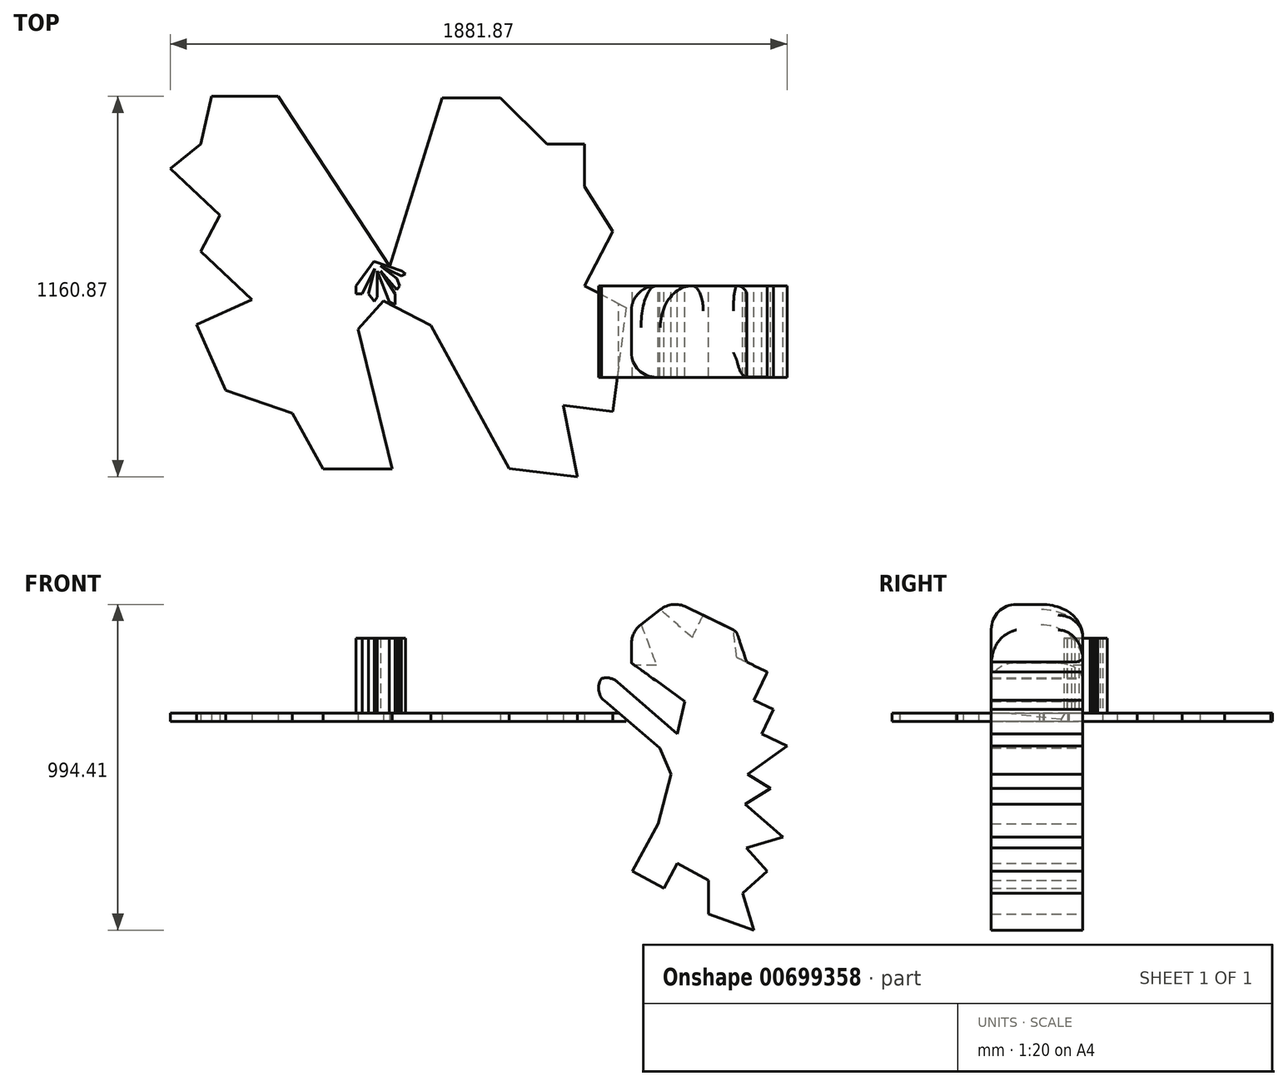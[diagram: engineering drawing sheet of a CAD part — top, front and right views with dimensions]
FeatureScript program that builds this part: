
annotation { "Feature Type Name" : "Feature", "Feature Type Description" : "" }
export const myFeature = defineFeature(function(context is Context, id is Id, definition is map)
    precondition{}
    {
        {
            var Q0;
            Q0=qCreatedBy(makeId("Top.planeOp"),FACE);
            var sketch = newSketch(context, id + "F0", { "sketchPlane" : qUnion([Q0])});
            skLineSegment(sketch, "E0", {"start": v(-30.37, 73.87) * mm, "end": v(-84.93, 0) * mm});
            skLineSegment(sketch, "E1", {"start": v(-84.93, 0) * mm, "end": v(-84.93, -24.22) * mm});
            skLineSegment(sketch, "E2", {"start": v(-84.93, -24.22) * mm, "end": v(-65.9, -24.22) * mm});
            skLineSegment(sketch, "E3", {"start": v(-65.9, -24.22) * mm, "end": v(-27.47, 52.56) * mm});
            skLineSegment(sketch, "E4", {"start": v(-27.47, 52.56) * mm, "end": v(-45.92, -24.95) * mm});
            skLineSegment(sketch, "E5", {"start": v(-45.92, -24.95) * mm, "end": v(-28.38, -47.2) * mm});
            skLineSegment(sketch, "E6", {"start": v(-28.38, -47.2) * mm, "end": v(-19.48, -35.16) * mm});
            skLineSegment(sketch, "E7", {"start": v(-19.48, -35.16) * mm, "end": v(-19.48, 44.64) * mm});
            skLineSegment(sketch, "E8", {"start": v(-19.48, 44.64) * mm, "end": v(16.74, -49.35) * mm});
            skLineSegment(sketch, "E9", {"start": v(16.74, -49.35) * mm, "end": v(35.46, -57.35) * mm});
            skLineSegment(sketch, "E10", {"start": v(35.46, -57.35) * mm, "end": v(35.46, -24.95) * mm});
            skLineSegment(sketch, "E11", {"start": v(35.46, -24.95) * mm, "end": v(-9.72, 44.64) * mm});
            skLineSegment(sketch, "E12", {"start": v(-9.72, 44.64) * mm, "end": v(40.42, -11.66) * mm});
            skLineSegment(sketch, "E13", {"start": v(40.42, -11.66) * mm, "end": v(49.03, 0) * mm});
            skLineSegment(sketch, "E14", {"start": v(49.03, 0) * mm, "end": v(40.42, 22.8) * mm});
            skLineSegment(sketch, "E15", {"start": v(40.42, 22.8) * mm, "end": v(-9.72, 59.82) * mm});
            skLineSegment(sketch, "E16", {"start": v(-9.72, 59.82) * mm, "end": v(53.76, 29.47) * mm});
            skLineSegment(sketch, "E17", {"start": v(53.76, 29.47) * mm, "end": v(67.14, 36.15) * mm});
            skLineSegment(sketch, "E18", {"start": v(67.14, 36.15) * mm, "end": v(55.65, 44.64) * mm});
            skLineSegment(sketch, "E19", {"start": v(55.65, 44.64) * mm, "end": v(-30.37, 73.87) * mm});
            skCircle(sketch, "E20", {"center": v(848.67, 52.41) * mm, "radius": 262.45 * mm});
            skCircle(sketch, "E21", {"center": v(612.08, -61.18) * mm, "radius": 272.09 * mm});
            skSolve(sketch);
        }
        {
            var Q0;
            Q0=makeQuery(id+"F0.imprint","IMPRINT",FACE,{"disambiguationData":[TD([[makeQuery(id+"F0.imprint","IMPRINT",EDGE,{"derivedFrom":sQuery(id+"F0.wireOp",EDGE,"E0")}),1.0]])]});
            extrude(context, id + "F1", {"entities" : qUnion([Q0]), "depth" : 254 * mm, "offsetDistance" : 25.4 * mm});
        }
        {
            var Q0;
            Q0=qCreatedBy(makeId("Top.planeOp"),FACE);
            var sketch = newSketch(context, id + "F2", { "sketchPlane" : qUnion([Q0])});
            skLineSegment(sketch, "E22", {"start": v(0, 0) * mm, "end": v(178.34, 573.44) * mm});
            skLineSegment(sketch, "E23", {"start": v(178.34, 573.44) * mm, "end": v(356.71, 573.44) * mm});
            skLineSegment(sketch, "E24", {"start": v(356.71, 573.44) * mm, "end": v(498.38, 432.3) * mm});
            skLineSegment(sketch, "E25", {"start": v(498.38, 432.3) * mm, "end": v(612.76, 432.3) * mm});
            skLineSegment(sketch, "E26", {"start": v(612.76, 432.3) * mm, "end": v(612.76, 303.27) * mm});
            skLineSegment(sketch, "E27", {"start": v(612.76, 303.27) * mm, "end": v(699.5, 165.4) * mm});
            skLineSegment(sketch, "E28", {"start": v(699.5, 165.4) * mm, "end": v(612.76, 0) * mm});
            skLineSegment(sketch, "E29", {"start": v(612.76, 0) * mm, "end": v(739.89, -66.67) * mm});
            skLineSegment(sketch, "E30", {"start": v(739.89, -66.67) * mm, "end": v(699.5, -384.6) * mm});
            skLineSegment(sketch, "E31", {"start": v(699.5, -384.6) * mm, "end": v(548.24, -365.4) * mm});
            skLineSegment(sketch, "E32", {"start": v(548.24, -365.4) * mm, "end": v(590.6, -582.87) * mm});
            skLineSegment(sketch, "E33", {"start": v(590.6, -582.87) * mm, "end": v(383.14, -558.17) * mm});
            skLineSegment(sketch, "E34", {"start": v(383.14, -558.17) * mm, "end": v(144.45, -121.46) * mm});
            skLineSegment(sketch, "E35", {"start": v(144.45, -121.46) * mm, "end": v(0, -45.7) * mm});
            skLineSegment(sketch, "E36", {"start": v(0, -45.7) * mm, "end": v(-77.82, -132.2) * mm});
            skLineSegment(sketch, "E37", {"start": v(-77.82, -132.2) * mm, "end": v(26.03, -559.4) * mm});
            skLineSegment(sketch, "E38", {"start": v(26.03, -559.4) * mm, "end": v(-184.42, -559.4) * mm});
            skLineSegment(sketch, "E39", {"start": v(-184.42, -559.4) * mm, "end": v(-278.79, -389.33) * mm});
            skLineSegment(sketch, "E40", {"start": v(-278.79, -389.33) * mm, "end": v(-482.47, -318.78) * mm});
            skLineSegment(sketch, "E41", {"start": v(-482.47, -318.78) * mm, "end": v(-571.43, -118.15) * mm});
            skLineSegment(sketch, "E42", {"start": v(-571.43, -118.15) * mm, "end": v(-402.06, -43.06) * mm});
            skLineSegment(sketch, "E43", {"start": v(-402.06, -43.06) * mm, "end": v(-557.53, 105.32) * mm});
            skLineSegment(sketch, "E44", {"start": v(-557.53, 105.32) * mm, "end": v(-499.66, 215.66) * mm});
            skLineSegment(sketch, "E45", {"start": v(-499.66, 215.66) * mm, "end": v(-651.09, 357.06) * mm});
            skLineSegment(sketch, "E46", {"start": v(-651.09, 357.06) * mm, "end": v(-557.53, 432.3) * mm});
            skLineSegment(sketch, "E47", {"start": v(-557.53, 432.3) * mm, "end": v(-524.67, 578) * mm});
            skLineSegment(sketch, "E48", {"start": v(-524.67, 578) * mm, "end": v(-322.06, 578) * mm});
            skLineSegment(sketch, "E49", {"start": v(-322.06, 578) * mm, "end": v(18.58, 59.74) * mm});
            skSolve(sketch);
        }
        {
            var Q0;
            {var subQ0=sQuery(id+"F2.wireOp",EDGE,"E23");Q0=makeQuery(id+"F2.imprint","IMPRINT",FACE,{"disambiguationData":[TD([[makeQuery(id+"F2.imprint","IMPRINT",EDGE,{"derivedFrom":subQ0}),-1.0]])]});}
            extrude(context, id + "F3", {"entities" : qUnion([Q0]), "operationType" : NewBodyOperationType.ADD, "depth" : 25.4 * mm, "offsetDistance" : 25.4 * mm});
        }
        {
            var Q0;
            Q0=qCreatedBy(makeId("Front.planeOp"),FACE);
            var sketch = newSketch(context, id + "F4", { "sketchPlane" : qUnion([Q0])});
            skLineSegment(sketch, "E50", {"start": v(1076.45, 274.56) * mm, "end": v(881.65, 370.25) * mm});
            skLineSegment(sketch, "E51", {"start": v(881.65, 370.25) * mm, "end": v(755.9, 273.4) * mm});
            skLineSegment(sketch, "E52", {"start": v(755.9, 273.4) * mm, "end": v(755.9, 178.66) * mm});
            skLineSegment(sketch, "E53", {"start": v(755.9, 178.66) * mm, "end": v(918.64, 61.21) * mm});
            skLineSegment(sketch, "E54", {"start": v(918.64, 61.21) * mm, "end": v(896.44, -38.41) * mm});
            skLineSegment(sketch, "E55", {"start": v(896.44, -38.41) * mm, "end": v(691.79, 139.03) * mm});
            skLineSegment(sketch, "E56", {"start": v(691.79, 139.03) * mm, "end": v(612.88, 114.95) * mm});
            skLineSegment(sketch, "E57", {"start": v(612.88, 114.95) * mm, "end": v(842.2, -81.93) * mm});
            skLineSegment(sketch, "E58", {"start": v(842.2, -81.93) * mm, "end": v(876.72, -160.94) * mm});
            skLineSegment(sketch, "E59", {"start": v(876.72, -160.94) * mm, "end": v(837.27, -312.29) * mm});
            skLineSegment(sketch, "E60", {"start": v(837.27, -312.29) * mm, "end": v(758.36, -457.18) * mm});
            skLineSegment(sketch, "E61", {"start": v(758.36, -457.18) * mm, "end": v(854.94, -509.78) * mm});
            skLineSegment(sketch, "E62", {"start": v(854.94, -509.78) * mm, "end": v(896.44, -433.55) * mm});
            skLineSegment(sketch, "E63", {"start": v(896.44, -433.55) * mm, "end": v(991, -485.05) * mm});
            skLineSegment(sketch, "E64", {"start": v(991, -485.05) * mm, "end": v(991, -588.43) * mm});
            skLineSegment(sketch, "E65", {"start": v(991, -588.43) * mm, "end": v(1129.6, -637.25) * mm});
            skLineSegment(sketch, "E66", {"start": v(1129.6, -637.25) * mm, "end": v(1095.94, -524.12) * mm});
            skLineSegment(sketch, "E67", {"start": v(1095.94, -524.12) * mm, "end": v(1170.57, -457.18) * mm});
            skLineSegment(sketch, "E68", {"start": v(1170.57, -457.18) * mm, "end": v(1107, -386.3) * mm});
            skLineSegment(sketch, "E69", {"start": v(1107, -386.3) * mm, "end": v(1218.74, -353.48) * mm});
            skLineSegment(sketch, "E70", {"start": v(1218.74, -353.48) * mm, "end": v(1103.14, -252.68) * mm});
            skLineSegment(sketch, "E71", {"start": v(1103.14, -252.68) * mm, "end": v(1180.2, -205.09) * mm});
            skLineSegment(sketch, "E72", {"start": v(1180.2, -205.09) * mm, "end": v(1110.37, -160.94) * mm});
            skLineSegment(sketch, "E73", {"start": v(1110.37, -160.94) * mm, "end": v(1230.78, -75.19) * mm});
            skLineSegment(sketch, "E74", {"start": v(1230.78, -75.19) * mm, "end": v(1153.72, -38.41) * mm});
            skLineSegment(sketch, "E75", {"start": v(1153.72, -38.41) * mm, "end": v(1189.4, 36.35) * mm});
            skLineSegment(sketch, "E76", {"start": v(1189.4, 36.35) * mm, "end": v(1129.6, 64.89) * mm});
            skLineSegment(sketch, "E77", {"start": v(1129.6, 64.89) * mm, "end": v(1170.72, 151.05) * mm});
            skLineSegment(sketch, "E78", {"start": v(1170.72, 151.05) * mm, "end": v(1107.85, 181.05) * mm});
            skLineSegment(sketch, "E79", {"start": v(1107.85, 181.05) * mm, "end": v(1076.45, 274.56) * mm});
            skSolve(sketch);
        }
        {
            var Q0;
            Q0=makeQuery(id+"F4.imprint","IMPRINT",FACE,{"disambiguationData":[TD([[makeQuery(id+"F4.imprint","IMPRINT",EDGE,{"derivedFrom":sQuery(id+"F4.wireOp",EDGE,"E50")}),1.0]])]});
            extrude(context, id + "F5", {"entities" : qUnion([Q0]), "operationType" : NewBodyOperationType.ADD, "depth" : 279.4 * mm, "offsetDistance" : 25.4 * mm});
        }
        {
            var Q0;
            Q0=makeQuery(id+"F5.opExtrude","CAP_EDGE",EDGE,{"disambiguationData":[OSD([sQuery(id+"F4.wireOp",EDGE,"E51")])],"isStart":true});
            fillet(context, id + "F6", {"entities" : qUnion([Q0]), "radius" : 127 * mm, "tangentPropagation" : true, "allowEdgeOverflow" : false});
        }
        {
            var Q0;
            Q0=makeQuery(id+"F5.opExtrude","SWEPT_EDGE",EDGE,{"disambiguationData":[OSD([sQuery(id+"F4.wireOp",EDGE,"E51"),sQuery(id+"F4.wireOp",EDGE,"E52")])]});
            fillet(context, id + "F7", {"entities" : qUnion([Q0]), "radius" : 76.2 * mm, "tangentPropagation" : true, "allowEdgeOverflow" : false});
        }
        {
            var Q0;
            Q0=makeQuery(id+"F5.opExtrude","SWEPT_EDGE",EDGE,{"disambiguationData":[OSD([sQuery(id+"F4.wireOp",EDGE,"E50"),sQuery(id+"F4.wireOp",EDGE,"E51")])]});
            fillet(context, id + "F8", {"entities" : qUnion([Q0]), "radius" : 76.2 * mm, "tangentPropagation" : true, "allowEdgeOverflow" : false});
        }
        {
            var Q0;
            Q0=makeQuery(id+"F5.opExtrude","SWEPT_EDGE",EDGE,{"disambiguationData":[OSD([sQuery(id+"F4.wireOp",EDGE,"E50"),sQuery(id+"F4.wireOp",EDGE,"E79")])]});
            fillet(context, id + "F9", {"entities" : qUnion([Q0]), "radius" : 25.4 * mm, "tangentPropagation" : true, "allowEdgeOverflow" : false});
        }
        {
            var Q0;
            Q0=makeQuery(id+"F5.opExtrude","CAP_EDGE",EDGE,{"disambiguationData":[OSD([sQuery(id+"F4.wireOp",EDGE,"E50")])],"isStart":false});
            fillet(context, id + "F10", {"entities" : qUnion([Q0]), "radius" : 76.2 * mm, "tangentPropagation" : true, "allowEdgeOverflow" : false});
        }
        {
            var Q0;
            Q0=makeQuery(id+"F5.opExtrude","SWEPT_EDGE",EDGE,{"disambiguationData":[OSD([sQuery(id+"F4.wireOp",EDGE,"E55"),sQuery(id+"F4.wireOp",EDGE,"E56")])]});
            fillet(context, id + "F11", {"entities" : qUnion([Q0]), "radius" : 50.8 * mm, "tangentPropagation" : true, "allowEdgeOverflow" : false});
        }
        {
            var Q0;
            Q0=makeQuery(id+"F5.opExtrude","SWEPT_EDGE",EDGE,{"disambiguationData":[OSD([sQuery(id+"F4.wireOp",EDGE,"E56"),sQuery(id+"F4.wireOp",EDGE,"E57")])]});
            fillet(context, id + "F12", {"entities" : qUnion([Q0]), "radius" : 50.8 * mm, "tangentPropagation" : true, "allowEdgeOverflow" : false});
        }
    });
